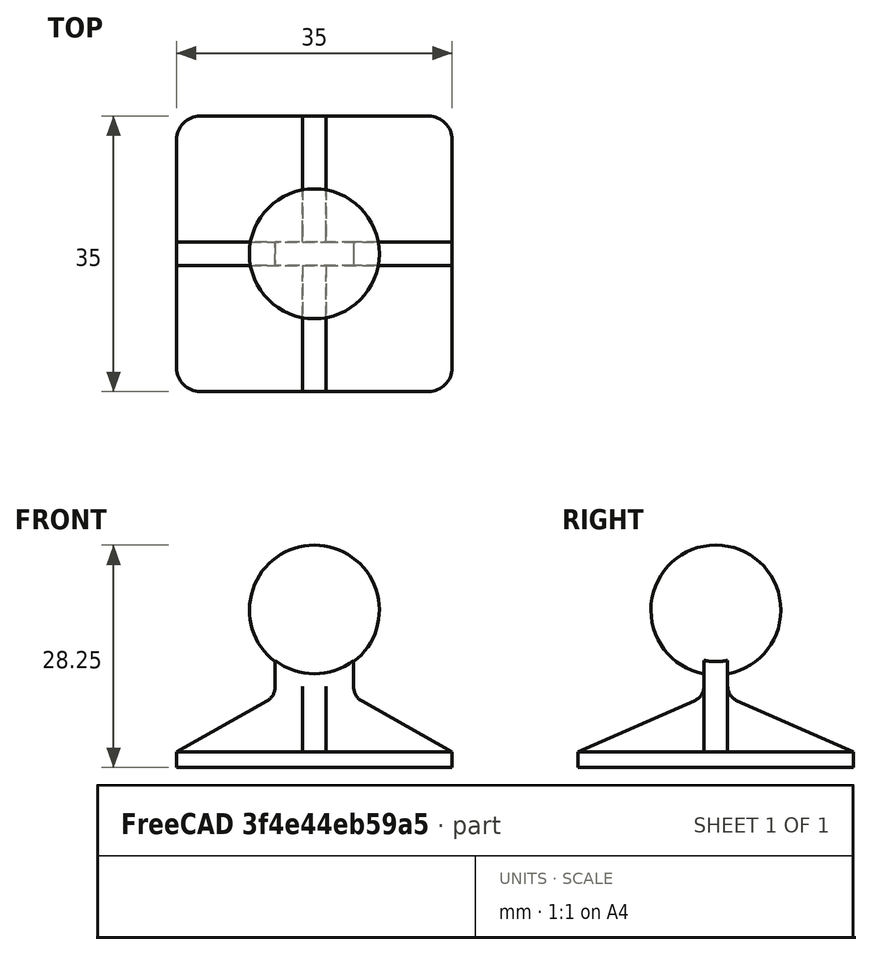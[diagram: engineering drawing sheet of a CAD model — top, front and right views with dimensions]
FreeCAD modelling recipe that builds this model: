
FCSTD DOCUMENT  (FreeCAD 2023.114R26244 +5346 (Git))
Label: ball_base
License: All rights reserved
LicenseURL: http://en.wikipedia.org/wiki/All_rights_reserved
objects: Sketcher::SketchObject×4, PartDesign::Pad×3, PartDesign::Fillet×2, Spreadsheet::Sheet×1, PartDesign::Revolution×1, PartDesign::Body×1, Mesh::Feature×1
note: 27 computed .brp shape members not serialized (recipe doc carries the construction recipe); baked Part::Feature solids carry a one-line shape summary decoded from their .brp

FEATURE [Sketcher::SketchObject] Sketch
  ArcFitTolerance = 1e-06
  AttachmentSupport = -> [XY_Plane]
  ExternalBSplineMaxDegree = 5
  ExternalBSplineTolerance = 0.0001
  FullyConstrained = true
  InternalTolerance = 1e-06
  InvalidShape = false
  MakeInternals = false
  MapMode = 5
  Support = -> [XY_Plane]
  TreeRank = 11
  ValidateShape = true
  expr: Constraints[11] = Spreadsheet.base_width
  sketch-geometry (5):
    g0: LineSegment StartX=-17.5 StartY=-17.5 StartZ=0 EndX=-17.5 EndY=17.5 EndZ=0
    g1: LineSegment StartX=-17.5 StartY=17.5 StartZ=0 EndX=17.5 EndY=17.5 EndZ=0
    g2: LineSegment StartX=17.5 StartY=17.5 StartZ=0 EndX=17.5 EndY=-17.5 EndZ=0
    g3: LineSegment StartX=17.5 StartY=-17.5 StartZ=0 EndX=-17.5 EndY=-17.5 EndZ=0
    g4: GeomPoint [constr] X=7e-16 Y=0 Z=0
  constraints (12):
    c: Coincident(g0,g1)
    c: Coincident(g1,g2)
    c: Coincident(g2,g3)
    c: Coincident(g3,g0)
    c: Horizontal(g1)
    c: Horizontal(g3)
    c: Vertical(g0)
    c: Vertical(g2)
    c: Symmetric(g1,g0,g4)
    c: Coincident(g4,g-1)
    c: Equal(g1,g2)
    c: DistanceX(g1,g1) = 35
FEATURE [Spreadsheet::Sheet] Spreadsheet
  PythonMode = false
  ShowCells = 0
  TreeRank = 12
  cells = A1=base_width; B1(base_width)=35; A2=ball_dia; B2(ball_dia)=16.5; A3=ball_height; B3(ball_height)=20; A4=pillar_dia; B4(pillar_dia)=10; A5=base_thk; B5(base_thk)=2; A6=web_thk; B6(web_thk)=3; A7=neck_height; B7(neck_height)=9
FEATURE [PartDesign::Pad] Pad
  AddSubType = 0
  AlongSketchNormal = false
  AutoTaperInnerAngle = true
  CheckUpToFaceLimits = true
  ClaimChildren = false
  Direction = (0,0,1)
  Fit = 0
  FitJoin = 0
  InnerFit = 0
  InnerFitJoin = 0
  InvalidShape = false
  Length = 2
  Length2 = 100
  Linearize = true
  NewSolid = false
  Profile = -> Sketch
  Refine = true
  Suppress = false
  TaperInnerAngle = 0
  TaperInnerAngleRev = 0
  TreeRank = 13
  Type = 0
  ValidateShape = true
  _ProfileBasedVersion = 1
  expr: Length = Spreadsheet.base_thk
FEATURE [Sketcher::SketchObject] Sketch001
  ArcFitTolerance = 1e-06
  AttachmentSupport = -> [XZ_Plane]
  ExternalBSplineMaxDegree = 5
  ExternalBSplineTolerance = 0.0001
  FullyConstrained = true
  InternalTolerance = 1e-06
  InvalidShape = false
  MakeInternals = false
  MapMode = 5
  Placement = pos=(0,0,0) rot=(1,0,0;1.5708rad)
  Support = -> [XZ_Plane]
  TreeRank = 14
  ValidateShape = true
  expr: Constraints[5] = Spreadsheet.ball_height
  expr: Constraints[6] = Spreadsheet.ball_dia
  sketch-geometry (2):
    g0: ArcOfCircle CenterX=0 CenterY=20 CenterZ=0 NormalX=0 NormalY=0 NormalZ=1 AngleXU=0 Radius=8.25 StartAngle=4.71239 EndAngle=7.85398
    g1: LineSegment StartX=0 StartY=28.25 StartZ=0 EndX=0 EndY=11.75 EndZ=0
  constraints (7):
    c: PointOnObject(g0,g-2)
    c: PointOnObject(g0,g-2)
    c: PointOnObject(g0,g-2)
    c: Coincident(g1,g0)
    c: Coincident(g1,g0)
    c: DistanceY(g-1,g0) = 20
    c: Diameter(g0) = 16.5
FEATURE [PartDesign::Revolution] Revolution
  AddSubType = 0
  Angle = 360
  Axis = (0,2e-16,1)
  Base = (0,0,0)
  BaseFeature = -> Pad
  ClaimChildren = false
  Fit = 0
  FitJoin = 0
  InnerFit = 0
  InnerFitJoin = 0
  InvalidShape = false
  Linearize = true
  NewSolid = false
  Profile = -> Sketch001
  ReferenceAxis = -> Sketch001 [V_Axis]
  Refine = true
  Reversed = true
  Suppress = false
  TreeRank = 15
  ValidateShape = true
  _ProfileBasedVersion = 1
FEATURE [Sketcher::SketchObject] Sketch002
  ArcFitTolerance = 1e-06
  AttachmentSupport = -> [XZ_Plane]
  ExternalBSplineMaxDegree = 5
  ExternalBSplineTolerance = 0.0001
  ExternalGeometry = -> [Revolution]
  FullyConstrained = true
  InternalTolerance = 1e-06
  InvalidShape = false
  MakeInternals = false
  MapMode = 5
  Placement = pos=(0,0,0) rot=(1,0,0;1.5708rad)
  Support = -> [XZ_Plane]
  TreeRank = 16
  ValidateShape = true
  expr: Constraints[11] = Spreadsheet.ball_height
  expr: Constraints[12] = Spreadsheet.neck_height
  expr: Constraints[14] = Spreadsheet.pillar_dia
  sketch-geometry (6):
    g0: LineSegment StartX=-17.5 StartY=2 StartZ=0 EndX=17.5 EndY=2 EndZ=0
    g1: LineSegment StartX=17.5 StartY=2 StartZ=0 EndX=5 EndY=9 EndZ=0
    g2: LineSegment StartX=5 StartY=9 StartZ=0 EndX=5 EndY=20 EndZ=0
    g3: LineSegment StartX=5 StartY=20 StartZ=0 EndX=-5 EndY=20 EndZ=0
    g4: LineSegment StartX=-5 StartY=20 StartZ=0 EndX=-5 EndY=9 EndZ=0
    g5: LineSegment StartX=-5 StartY=9 StartZ=0 EndX=-17.5 EndY=2 EndZ=0
  constraints (15):
    c: Coincident(g-3,g0)
    c: Coincident(g0,g-3)
    c: Coincident(g0,g1)
    c: Coincident(g1,g2)
    c: Vertical(g2)
    c: Coincident(g2,g3)
    c: Coincident(g3,g4)
    c: Vertical(g4)
    c: Coincident(g4,g5)
    c: Coincident(g5,g0)
    c: Symmetric(g3,g2,g-2)
    c: DistanceY(g-1,g3) = 20
    c: DistanceY(g-1,g4) = 9
    c: Equal(g4,g2)
    c: DistanceX(g3,g3) = 10
FEATURE [PartDesign::Pad] Pad001
  AddSubType = 0
  AlongSketchNormal = false
  AutoTaperInnerAngle = true
  BaseFeature = -> Revolution
  CheckUpToFaceLimits = true
  ClaimChildren = false
  Direction = (0,-1,2e-16)
  Fit = 0
  FitJoin = 0
  InnerFit = 0
  InnerFitJoin = 0
  InvalidShape = false
  Length = 3
  Length2 = 100
  Linearize = true
  Midplane = true
  NewSolid = false
  Profile = -> Sketch002
  Refine = true
  Suppress = false
  TaperInnerAngle = 0
  TaperInnerAngleRev = 0
  TreeRank = 17
  Type = 0
  ValidateShape = true
  _ProfileBasedVersion = 1
  expr: Length = Spreadsheet.web_thk
FEATURE [Sketcher::SketchObject] Sketch003
  ArcFitTolerance = 1e-06
  AttachmentSupport = -> [YZ_Plane]
  ExternalBSplineMaxDegree = 5
  ExternalBSplineTolerance = 0.0001
  ExternalGeometry = -> [Pad001]
  FullyConstrained = true
  InternalTolerance = 1e-06
  InvalidShape = false
  MakeInternals = false
  MapMode = 5
  Placement = pos=(0,0,0) rot=(0.57735,0.57735,0.57735;2.0944rad)
  Support = -> [YZ_Plane]
  TreeRank = 18
  ValidateShape = true
  sketch-geometry (4):
    g0: LineSegment StartX=-17.5 StartY=2 StartZ=0 EndX=-1.5 EndY=9 EndZ=0
    g1: LineSegment StartX=-1.5 StartY=9 StartZ=0 EndX=1.5 EndY=9 EndZ=0
    g2: LineSegment StartX=1.5 StartY=9 StartZ=0 EndX=17.5 EndY=2 EndZ=0
    g3: LineSegment StartX=17.5 StartY=2 StartZ=0 EndX=-17.5 EndY=2 EndZ=0
  constraints (8):
    c: Coincident(g-3,g0)
    c: Coincident(g0,g-5)
    c: Coincident(g0,g1)
    c: Coincident(g1,g-5)
    c: Coincident(g1,g2)
    c: Coincident(g2,g-4)
    c: Coincident(g2,g3)
    c: Coincident(g3,g0)
FEATURE [PartDesign::Pad] Pad002
  AddSubType = 0
  AlongSketchNormal = false
  AutoTaperInnerAngle = true
  BaseFeature = -> Pad001
  CheckUpToFaceLimits = true
  ClaimChildren = false
  Direction = (1,-2e-16,3e-16)
  Fit = 0
  FitJoin = 0
  InnerFit = 0
  InnerFitJoin = 0
  InvalidShape = false
  Length = 3
  Length2 = 100
  Linearize = true
  Midplane = true
  NewSolid = false
  Profile = -> Sketch003
  Refine = true
  Suppress = false
  TaperInnerAngle = 0
  TaperInnerAngleRev = 0
  TreeRank = 19
  Type = 0
  ValidateShape = true
  _ProfileBasedVersion = 1
  expr: Length = Spreadsheet.web_thk
FEATURE [PartDesign::Fillet] Fillet
  AddSubType = 0
  Base = -> Pad002 [Edge1,Edge2,Edge12,Edge7]
  BaseFeature = -> Pad002
  InvalidShape = false
  NewSolid = false
  Radius = 3
  Refine = true
  SupportTransform = false
  Suppress = false
  TreeRank = 20
  ValidateShape = true
FEATURE [PartDesign::Fillet] Fillet001
  AddSubType = 0
  Base = -> Fillet [Edge24,Edge41,Edge63,Edge50]
  BaseFeature = -> Fillet
  InvalidShape = false
  NewSolid = false
  Radius = 2
  Refine = true
  SupportTransform = false
  Suppress = false
  TreeRank = 21
  ValidateShape = true
FEATURE [PartDesign::Body] Body
  AutoGroupSolids = false
  ClaimAllChildren = false
  ExportMode = 0
  Group = -> [Sketch,Pad,Sketch001,Revolution,Sketch002,Pad001,Sketch003,Pad002,Fillet,Fillet001]
  InvalidShape = false
  Origin = -> Origin
  Tip = -> Fillet001
  TreeRank = 10
  ValidateShape = true
  _ExportChildren = -> [Pad,Revolution,Pad001,Pad002,Fillet,Fillet001]
  _GroupVersion = 1
FEATURE [Mesh::Feature] Mesh  label="ball_base_1"
  TreeRank = 22
